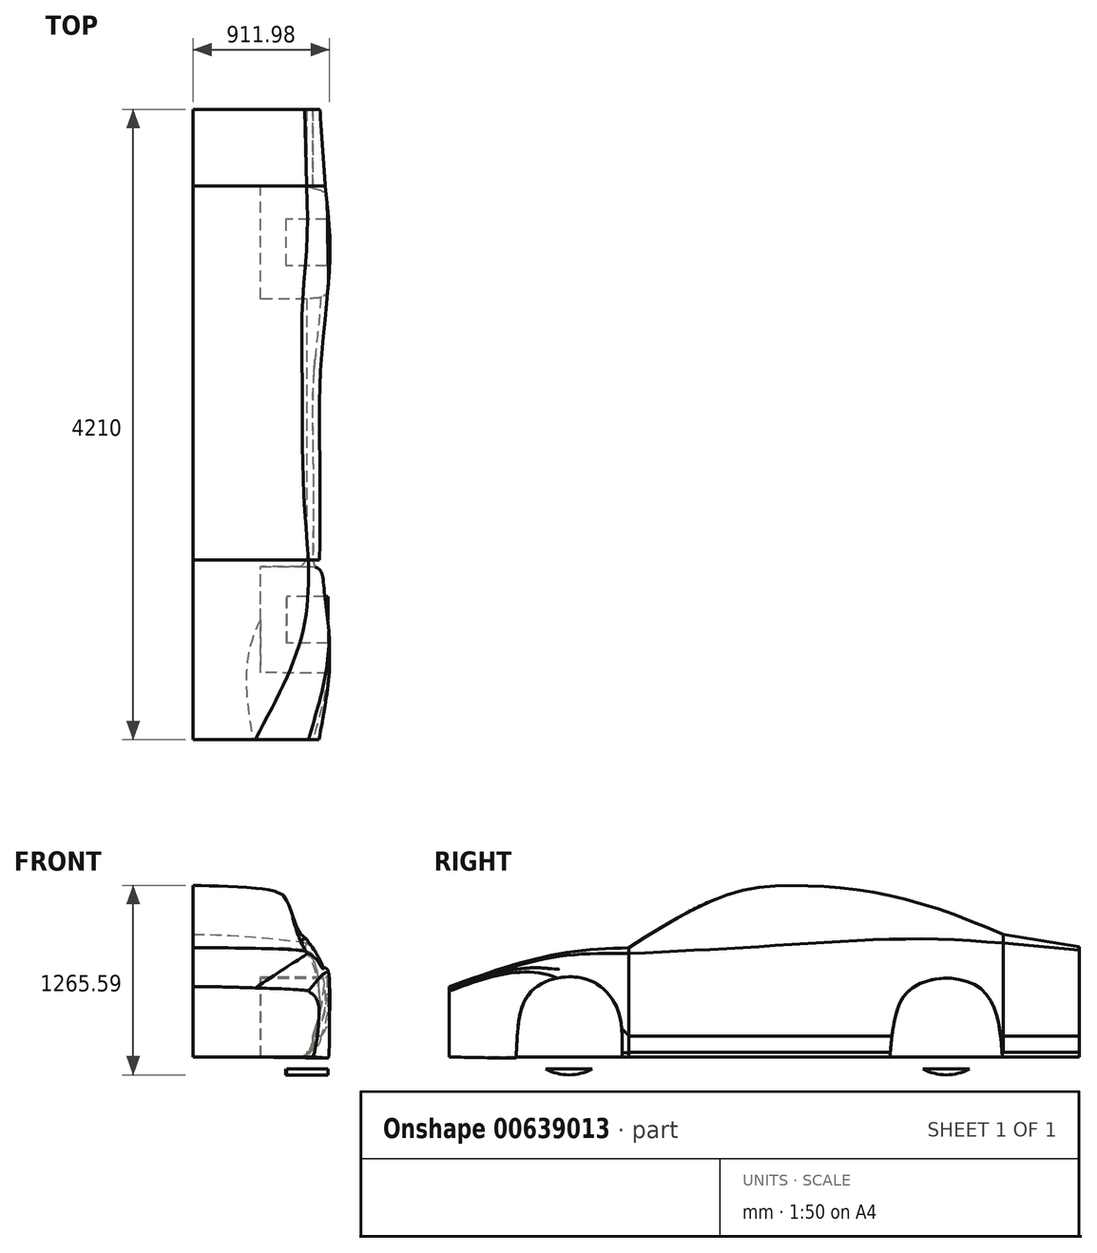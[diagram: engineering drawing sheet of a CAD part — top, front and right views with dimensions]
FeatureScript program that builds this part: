
annotation { "Feature Type Name" : "Feature", "Feature Type Description" : "" }
export const myFeature = defineFeature(function(context is Context, id is Id, definition is map)
    precondition{}
    {
        {
            var Q0;
            Q0=qCreatedBy(makeId("Front.planeOp"),FACE);
            cPlane(context, id + "F0", {"entities" : qUnion([Q0]), "cplaneType" : CPlaneType.OFFSET, "offset" : 1550 * mm, "width" : 150 * mm, "height" : 150 * mm});
        }
        {
            var Q0;
            Q0=qCreatedBy(makeId("Front.planeOp"),FACE);
            var sketch = newSketch(context, id + "F1", { "sketchPlane" : qUnion([Q0])});
            skLineSegment(sketch, "E0", {"start": v(0, 0) * mm, "end": v(0, 1145) * mm});
            skFitSpline(sketch, "E1", {"points": [v(0, 1145) * mm, v(530, 1110) * mm, v(584.13, 1089.1) * mm, v(618.69, 1056.85) * mm, v(730, 755) * mm], "startDerivative": vector(1143.35, -6.37) * mm, "endDerivative": vector(344.8, -611.59) * mm});
            skFitSpline(sketch, "E2", {"points": [v(730, 755) * mm, v(756.9, 725.08) * mm, v(802.98, 635.22) * mm, v(840, 470) * mm, v(839.87, 278.1) * mm, v(800, 140) * mm], "startDerivative": vector(297.23, -793.68) * mm, "endDerivative": vector(-278.77, -815.3) * mm});
            skFitSpline(sketch, "E3", {"points": [v(800, 140) * mm, v(794.56, 59.98) * mm, v(760, 30) * mm], "startDerivative": vector(4.47, -175.02) * mm, "endDerivative": vector(-95.38, 8.42) * mm});
            skLineSegment(sketch, "E4", {"start": v(760, 30) * mm, "end": v(760, 0) * mm});
            skLineSegment(sketch, "E5", {"start": v(760, 0) * mm, "end": v(0, 0) * mm});
            skSolve(sketch);
        }
        {
            var Q0;
            Q0=qCreatedBy(id+"F0.planeOp",FACE);
            var sketch = newSketch(context, id + "F2", { "sketchPlane" : qUnion([Q0])});
            skLineSegment(sketch, "E6.bottom", {"start": v(625, 200) * mm, "end": v(900, 200) * mm});
            skLineSegment(sketch, "E6.top", {"start": v(625, -120) * mm, "end": v(900, -120) * mm});
            skLineSegment(sketch, "E6.left", {"start": v(625, 200) * mm, "end": v(625, -120) * mm});
            skLineSegment(sketch, "E6.right", {"start": v(900, 200) * mm, "end": v(900, -120) * mm});
            skSolve(sketch);
        }
        {
            var Q0;
            Q0=makeQuery(id+"F2.imprint","IMPRINT",FACE,{"disambiguationData":[TD([[makeQuery(id+"F2.imprint","IMPRINT",EDGE,{"derivedFrom":sQuery(id+"F2.wireOp",EDGE,"E6.bottom")}),-1.0]])]});
            var Q1;
            Q1=sQuery(id+"F2.wireOp",EDGE,"E6.bottom");
            revolve(context, id + "F3", {"entities" : qUnion([Q0]), "axis" : qUnion([Q1]), "revolveType" : RevolveType.FULL});
        }
        {
            var Q0;
            Q0=qCreatedBy(makeId("Front.planeOp"),FACE);
            cPlane(context, id + "F4", {"entities" : qUnion([Q0]), "cplaneType" : CPlaneType.OFFSET, "offset" : 970 * mm, "oppositeDirection" : true, "width" : 150 * mm, "height" : 150 * mm});
        }
        {
            var Q0;
            Q0=qCreatedBy(id+"F4.planeOp",FACE);
            var sketch = newSketch(context, id + "F5", { "sketchPlane" : qUnion([Q0])});
            skLineSegment(sketch, "E7.bottom", {"start": v(620, -120) * mm, "end": v(895, -120) * mm});
            skLineSegment(sketch, "E7.top", {"start": v(620, 200) * mm, "end": v(895, 200) * mm});
            skLineSegment(sketch, "E7.left", {"start": v(620, -120) * mm, "end": v(620, 200) * mm});
            skLineSegment(sketch, "E7.right", {"start": v(895, -120) * mm, "end": v(895, 200) * mm});
            skSolve(sketch);
        }
        {
            var Q0;
            Q0 = qSketchRegion(id + "F5", true);
            var Q1;
            Q1=sQuery(id+"F5.wireOp",EDGE,"E7.top");
            revolve(context, id + "F6", {"entities" : qUnion([Q0]), "axis" : qUnion([Q1]), "revolveType" : RevolveType.FULL});
        }
        {
            var Q0;
            Q0=qCreatedBy(makeId("Front.planeOp"),FACE);
            cPlane(context, id + "F7", {"entities" : qUnion([Q0]), "cplaneType" : CPlaneType.OFFSET, "offset" : 560 * mm, "oppositeDirection" : true, "width" : 150 * mm, "height" : 150 * mm});
        }
        {
            var Q0;
            Q0=qCreatedBy(makeId("Front.planeOp"),FACE);
            cPlane(context, id + "F8", {"entities" : qUnion([Q0]), "cplaneType" : CPlaneType.OFFSET, "offset" : 1350 * mm, "oppositeDirection" : true, "width" : 150 * mm, "height" : 150 * mm});
        }
        {
            var Q0;
            Q0=qCreatedBy(makeId("Front.planeOp"),FACE);
            cPlane(context, id + "F9", {"entities" : qUnion([Q0]), "cplaneType" : CPlaneType.OFFSET, "offset" : 400 * mm, "width" : 150 * mm, "height" : 150 * mm});
        }
        {
            var Q0;
            Q0=qCreatedBy(makeId("Front.planeOp"),FACE);
            cPlane(context, id + "F10", {"entities" : qUnion([Q0]), "cplaneType" : CPlaneType.OFFSET, "offset" : 1150 * mm, "width" : 150 * mm, "height" : 150 * mm});
        }
        {
            var Q0;
            Q0=qCreatedBy(makeId("Front.planeOp"),FACE);
            cPlane(context, id + "F11", {"entities" : qUnion([Q0]), "cplaneType" : CPlaneType.OFFSET, "offset" : 2350 * mm, "width" : 150 * mm, "height" : 150 * mm});
        }
        {
            var Q0;
            Q0=qCreatedBy(makeId("Front.planeOp"),FACE);
            cPlane(context, id + "F12", {"entities" : qUnion([Q0]), "cplaneType" : CPlaneType.OFFSET, "offset" : 1860 * mm, "oppositeDirection" : true, "width" : 150 * mm, "height" : 150 * mm});
        }
        {
            var Q0;
            Q0=qCreatedBy(id+"F7.planeOp",FACE);
            var sketch = newSketch(context, id + "F13", { "sketchPlane" : qUnion([Q0])});
            skLineSegment(sketch, "E8", {"start": v(0, 0) * mm, "end": v(0, 1085) * mm});
            skFitSpline(sketch, "E9", {"points": [v(0, 1085) * mm, v(540, 1040) * mm, v(598.07, 1017.26) * mm, v(651.48, 958.23) * mm, v(730, 785) * mm], "startDerivative": vector(1143.35, -6.37) * mm, "endDerivative": vector(344.8, -611.59) * mm});
            skFitSpline(sketch, "E10", {"points": [v(730, 785) * mm, v(784.3, 715.18) * mm, v(812.94, 650.48) * mm, v(880, 495) * mm, v(886.1, 287.13) * mm, v(850, 140) * mm], "startDerivative": vector(297.23, -793.68) * mm, "endDerivative": vector(-278.77, -815.3) * mm});
            skFitSpline(sketch, "E11", {"points": [v(850, 140) * mm, v(820.63, 59.58) * mm, v(760, 30) * mm], "startDerivative": vector(-15.58, -265.91) * mm, "endDerivative": vector(-95.38, 8.42) * mm});
            skLineSegment(sketch, "E12", {"start": v(760, 30) * mm, "end": v(760, 0) * mm});
            skLineSegment(sketch, "E13", {"start": v(760, 0) * mm, "end": v(0, 0) * mm});
            skSolve(sketch);
        }
        {
            var Q0;
            Q0=qCreatedBy(id+"F8.planeOp",FACE);
            var sketch = newSketch(context, id + "F14", { "sketchPlane" : qUnion([Q0])});
            skLineSegment(sketch, "E14", {"start": v(0, 0) * mm, "end": v(0, 820) * mm});
            skFitSpline(sketch, "E15", {"points": [v(0, 820) * mm, v(535, 790) * mm, v(651.92, 777.4) * mm, v(760, 760) * mm], "startDerivative": vector(1143.35, -6.37) * mm, "endDerivative": vector(724.01, -187.44) * mm});
            skFitSpline(sketch, "E16", {"points": [v(760, 760) * mm, v(845.07, 637.93) * mm, v(859.36, 579.22) * mm, v(880, 445) * mm, v(871.26, 287.38) * mm, v(800, 140) * mm], "startDerivative": vector(508.67, -188.24) * mm, "endDerivative": vector(-462.29, -801.37) * mm});
            skFitSpline(sketch, "E17", {"points": [v(800, 140) * mm, v(788.46, 71.77) * mm, v(760, 30) * mm], "startDerivative": vector(4.47, -175.02) * mm, "endDerivative": vector(-95.38, 8.42) * mm});
            skLineSegment(sketch, "E18", {"start": v(760, 30) * mm, "end": v(760, 0) * mm});
            skLineSegment(sketch, "E19", {"start": v(760, 0) * mm, "end": v(0, 0) * mm});
            skSolve(sketch);
        }
        {
            var Q0;
            Q0=qCreatedBy(id+"F10.planeOp",FACE);
            var sketch = newSketch(context, id + "F15", { "sketchPlane" : qUnion([Q0])});
            skLineSegment(sketch, "E20", {"start": v(0, 0) * mm, "end": v(0, 730) * mm});
            skFitSpline(sketch, "E21", {"points": [v(0, 730) * mm, v(750, 705) * mm, v(770, 690) * mm], "startDerivative": vector(1143.35, -6.37) * mm, "endDerivative": vector(152.81, -146.87) * mm});
            skFitSpline(sketch, "E22", {"points": [v(770, 690) * mm, v(811.7, 628.13) * mm, v(830.71, 547.8) * mm, v(840, 445) * mm, v(842.46, 274.78) * mm, v(800, 140) * mm], "startDerivative": vector(202.73, -222.8) * mm, "endDerivative": vector(-278.77, -815.3) * mm});
            skFitSpline(sketch, "E23", {"points": [v(800, 140) * mm, v(795.45, 63.03) * mm, v(760, 30) * mm], "startDerivative": vector(4.47, -175.02) * mm, "endDerivative": vector(-95.38, 8.42) * mm});
            skLineSegment(sketch, "E24", {"start": v(760, 30) * mm, "end": v(760, 0) * mm});
            skLineSegment(sketch, "E25", {"start": v(760, 0) * mm, "end": v(0, 0) * mm});
            skSolve(sketch);
        }
        {
            var Q0;
            Q0=qCreatedBy(id+"F11.planeOp",FACE);
            var sketch = newSketch(context, id + "F16", { "sketchPlane" : qUnion([Q0])});
            skLineSegment(sketch, "E26", {"start": v(0, 0) * mm, "end": v(0, 470) * mm});
            skFitSpline(sketch, "E27", {"points": [v(0, 470) * mm, v(450, 460) * mm, v(770, 440) * mm], "startDerivative": vector(1143.35, -6.37) * mm, "endDerivative": vector(46.44, -65.76) * mm});
            skFitSpline(sketch, "E28", {"points": [v(770, 440) * mm, v(812.39, 405.96) * mm, v(832.27, 368.84) * mm, v(840, 330) * mm, v(839.96, 276.13) * mm, v(800, 0) * mm], "startDerivative": vector(382.07, -290.8) * mm, "endDerivative": vector(-278.77, -815.3) * mm});
            skLineSegment(sketch, "E29", {"start": v(0, 0) * mm, "end": v(800, 0) * mm});
            skSolve(sketch);
        }
        {
            var Q0;
            Q0=qCreatedBy(id+"F12.planeOp",FACE);
            var sketch = newSketch(context, id + "F17", { "sketchPlane" : qUnion([Q0])});
            skLineSegment(sketch, "E30", {"start": v(0, 0) * mm, "end": v(0, 735) * mm});
            skFitSpline(sketch, "E31", {"points": [v(0, 735) * mm, v(530, 730) * mm, v(582.75, 730) * mm, v(659.56, 727.7) * mm, v(745, 715) * mm], "startDerivative": vector(1143.35, -6.37) * mm, "endDerivative": vector(632.21, -134.94) * mm});
            skFitSpline(sketch, "E32", {"points": [v(745, 715) * mm, v(807.27, 650.9) * mm, v(833.85, 526.82) * mm, v(840, 445) * mm, v(845.67, 275.72) * mm, v(800, 140) * mm], "startDerivative": vector(1028.7, -300.5) * mm, "endDerivative": vector(-278.77, -815.3) * mm});
            skFitSpline(sketch, "E33", {"points": [v(800, 140) * mm, v(789.54, 60.07) * mm, v(760, 30) * mm], "startDerivative": vector(4.47, -175.02) * mm, "endDerivative": vector(-95.38, 8.42) * mm});
            skLineSegment(sketch, "E34", {"start": v(760, 30) * mm, "end": v(760, 0) * mm});
            skLineSegment(sketch, "E35", {"start": v(760, 0) * mm, "end": v(0, 0) * mm});
            skSolve(sketch);
        }
        {
            var Q0;
            Q0=qCreatedBy(id+"F9.planeOp",FACE);
            var sketch = newSketch(context, id + "F18", { "sketchPlane" : qUnion([Q0])});
            skLineSegment(sketch, "E36", {"start": v(0, 0) * mm, "end": v(0, 1110) * mm});
            skFitSpline(sketch, "E37", {"points": [v(0, 1110) * mm, v(560, 1075) * mm, v(615.63, 1021.07) * mm, v(663.68, 929.16) * mm, v(730, 730) * mm], "startDerivative": vector(1143.35, -6.37) * mm, "endDerivative": vector(344.8, -611.59) * mm});
            skFitSpline(sketch, "E38", {"points": [v(730, 730) * mm, v(749.76, 710.26) * mm, v(794.76, 631.69) * mm, v(840, 445) * mm, v(839.76, 272.77) * mm, v(800, 140) * mm], "startDerivative": vector(196.18, -495.16) * mm, "endDerivative": vector(-278.77, -815.3) * mm});
            skFitSpline(sketch, "E39", {"points": [v(800, 140) * mm, v(792.5, 63.03) * mm, v(760, 30) * mm], "startDerivative": vector(4.47, -175.02) * mm, "endDerivative": vector(-95.38, 8.42) * mm});
            skLineSegment(sketch, "E40", {"start": v(760, 30) * mm, "end": v(760, 0) * mm});
            skLineSegment(sketch, "E41", {"start": v(760, 0) * mm, "end": v(0, 0) * mm});
            skSolve(sketch);
        }
        {
            var Q0;
            Q0=qCreatedBy(makeId("Right.planeOp"),FACE);
            cPlane(context, id + "F19", {"entities" : qUnion([Q0]), "cplaneType" : CPlaneType.OFFSET, "offset" : 450 * mm, "width" : 150 * mm, "height" : 150 * mm});
        }
        {
            var Q0;
            Q0=qCreatedBy(id+"F19.planeOp",FACE);
            var sketch = newSketch(context, id + "F20", { "sketchPlane" : qUnion([Q0])});
            skLineSegment(sketch, "E42", {"start": v(-1910, -80) * mm, "end": v(-1190, -80) * mm});
            skFitSpline(sketch, "E43", {"points": [v(-1910, -80) * mm, v(-1873.46, 304.56) * mm, v(-1761.3, 472.8) * mm, v(-1550.2, 535) * mm, v(-1349.53, 477.6) * mm, v(-1210.13, 267.71) * mm, v(-1190, -80) * mm], "startDerivative": vector(210.4, 2294.01) * mm, "endDerivative": vector(215.54, -1912.7) * mm});
            skSolve(sketch);
        }
        {
            var Q0;
            Q0=qCreatedBy(id+"F19.planeOp",FACE);
            var sketch = newSketch(context, id + "F21", { "sketchPlane" : qUnion([Q0])});
            skLineSegment(sketch, "E44", {"start": v(590, -80) * mm, "end": v(1350, -80) * mm});
            skFitSpline(sketch, "E45", {"points": [v(590, -80) * mm, v(621.22, 227.66) * mm, v(704.54, 426.33) * mm, v(938.25, 525) * mm, v(1202.83, 453.57) * mm, v(1316.59, 238.87) * mm, v(1350, -80) * mm], "startDerivative": vector(112.36, 2250.75) * mm, "endDerivative": vector(158.4, -2185.73) * mm});
            skSolve(sketch);
        }
        {
            var Q0;
            Q0=qCreatedBy(id+"F0.planeOp",FACE);
            var sketch = newSketch(context, id + "F22", { "sketchPlane" : qUnion([Q0])});
            skLineSegment(sketch, "E46", {"start": v(0, 0) * mm, "end": v(0, 700) * mm});
            skFitSpline(sketch, "E47", {"points": [v(0, 700) * mm, v(750, 680) * mm], "startDerivative": vector(1143.35, -6.37) * mm, "endDerivative": vector(148.7, -37.78) * mm});
            skFitSpline(sketch, "E48", {"points": [v(750, 680) * mm, v(858.98, 599.13) * mm, v(889.18, 565.47) * mm, v(900, 535) * mm, v(900.14, 324.76) * mm, v(900, 0) * mm], "startDerivative": vector(1067.2, -245.33) * mm, "endDerivative": vector(-32, -970.74) * mm});
            skLineSegment(sketch, "E49", {"start": v(900, 0) * mm, "end": v(0, 0) * mm});
            skSolve(sketch);
        }
        {
            var Q0;
            Q0=qCreatedBy(id+"F4.planeOp",FACE);
            var sketch = newSketch(context, id + "F23", { "sketchPlane" : qUnion([Q0])});
            skLineSegment(sketch, "E50", {"start": v(0, 0) * mm, "end": v(0, 970) * mm});
            skFitSpline(sketch, "E51", {"points": [v(0, 970) * mm, v(597.63, 885.63) * mm, v(760, 785) * mm], "startDerivative": vector(1143.35, -6.37) * mm, "endDerivative": vector(553.52, -342.02) * mm});
            skFitSpline(sketch, "E52", {"points": [v(760, 785) * mm, v(848.18, 644.9) * mm, v(879.7, 557.62) * mm, v(900, 525) * mm, v(913.26, 334.57) * mm, v(850, 140) * mm], "startDerivative": vector(497.88, -841.7) * mm, "endDerivative": vector(-591.76, -566.9) * mm});
            skFitSpline(sketch, "E53", {"points": [v(850, 140) * mm, v(792.06, 63.39) * mm, v(760, 30) * mm], "startDerivative": vector(4.47, -175.02) * mm, "endDerivative": vector(-95.38, 8.42) * mm});
            skLineSegment(sketch, "E54", {"start": v(760, 30) * mm, "end": v(760, 0) * mm});
            skLineSegment(sketch, "E55", {"start": v(760, 0) * mm, "end": v(0, 0) * mm});
            skSolve(sketch);
        }
        {
            var Q0;
            Q0=makeQuery(id+"F17.imprint","IMPRINT",FACE,{"disambiguationData":[TD([[makeQuery(id+"F17.imprint","IMPRINT",EDGE,{"derivedFrom":sQuery(id+"F17.wireOp",EDGE,"E30")}),-1.0]])]});
            var Q1;
            Q1=makeQuery(id+"F14.imprint","IMPRINT",FACE,{"disambiguationData":[TD([[makeQuery(id+"F14.imprint","IMPRINT",EDGE,{"derivedFrom":sQuery(id+"F14.wireOp",EDGE,"E14")}),-1.0]])]});
            loft(context, id + "F24", {"sheetProfilesArray" : [{ "sheetProfileEntities" : qUnion([Q0]) }, { "sheetProfileEntities" : qUnion([Q1]) }]});
        }
        {
            var Q1;
            Q1=makeQuery(id+"F14.imprint","IMPRINT",FACE,{"disambiguationData":[TD([[makeQuery(id+"F14.imprint","IMPRINT",EDGE,{"derivedFrom":sQuery(id+"F14.wireOp",EDGE,"E14")}),-1.0]])]});
            var Q2;
            Q2=makeQuery(id+"F23.imprint","IMPRINT",FACE,{"disambiguationData":[TD([[makeQuery(id+"F23.imprint","IMPRINT",EDGE,{"derivedFrom":sQuery(id+"F23.wireOp",EDGE,"E50")}),-1.0]])]});
            var Q3;
            Q3=makeQuery(id+"F13.imprint","IMPRINT",FACE,{"disambiguationData":[TD([[makeQuery(id+"F13.imprint","IMPRINT",EDGE,{"derivedFrom":sQuery(id+"F13.wireOp",EDGE,"E8")}),-1.0]])]});
            var Q4;
            Q4=makeQuery(id+"F1.imprint","IMPRINT",FACE,{"disambiguationData":[TD([[makeQuery(id+"F1.imprint","IMPRINT",EDGE,{"derivedFrom":sQuery(id+"F1.wireOp",EDGE,"E0")}),-1.0]])]});
            var Q5;
            Q5=makeQuery(id+"F18.imprint","IMPRINT",FACE,{"disambiguationData":[TD([[makeQuery(id+"F18.imprint","IMPRINT",EDGE,{"derivedFrom":sQuery(id+"F18.wireOp",EDGE,"E36")}),-1.0]])]});
            var Q6;
            Q6=makeQuery(id+"F15.imprint","IMPRINT",FACE,{"disambiguationData":[TD([[makeQuery(id+"F15.imprint","IMPRINT",EDGE,{"derivedFrom":sQuery(id+"F15.wireOp",EDGE,"E20")}),-1.0]])]});
            loft(context, id + "F25", {"operationType" : NewBodyOperationType.ADD, "sheetProfilesArray" : [{ "sheetProfileEntities" : qUnion([Q1]) }, { "sheetProfileEntities" : qUnion([Q2]) }, { "sheetProfileEntities" : qUnion([Q3]) }, { "sheetProfileEntities" : qUnion([Q4]) }, { "sheetProfileEntities" : qUnion([Q5]) }, { "sheetProfileEntities" : qUnion([Q6]) }]});
        }
        {
            var Q1;
            Q1=makeQuery(id+"F15.imprint","IMPRINT",FACE,{"disambiguationData":[TD([[makeQuery(id+"F15.imprint","IMPRINT",EDGE,{"derivedFrom":sQuery(id+"F15.wireOp",EDGE,"E20")}),-1.0]])]});
            var Q2;
            Q2=makeQuery(id+"F22.imprint","IMPRINT",FACE,{"disambiguationData":[TD([[makeQuery(id+"F22.imprint","IMPRINT",EDGE,{"derivedFrom":sQuery(id+"F22.wireOp",EDGE,"E46")}),-1.0]])]});
            var Q3;
            Q3=makeQuery(id+"F16.imprint","IMPRINT",FACE,{"disambiguationData":[TD([[makeQuery(id+"F16.imprint","IMPRINT",EDGE,{"derivedFrom":sQuery(id+"F16.wireOp",EDGE,"E26")}),-1.0]])]});
            loft(context, id + "F26", {"operationType" : NewBodyOperationType.ADD, "sheetProfilesArray" : [{ "sheetProfileEntities" : qUnion([Q1]) }, { "sheetProfileEntities" : qUnion([Q2]) }, { "sheetProfileEntities" : qUnion([Q3]) }]});
        }
        {
            var Q0;
            Q0 = qSketchRegion(id + "F21", true);
            extrude(context, id + "F27", {"entities" : qUnion([Q0]), "operationType" : NewBodyOperationType.REMOVE, "depth" : 500 * mm, "offsetDistance" : 25 * mm});
        }
        {
            var Q0;
            Q0 = qSketchRegion(id + "F20", true);
            extrude(context, id + "F28", {"entities" : qUnion([Q0]), "operationType" : NewBodyOperationType.REMOVE, "depth" : 500 * mm, "offsetDistance" : 25 * mm});
        }
    });
